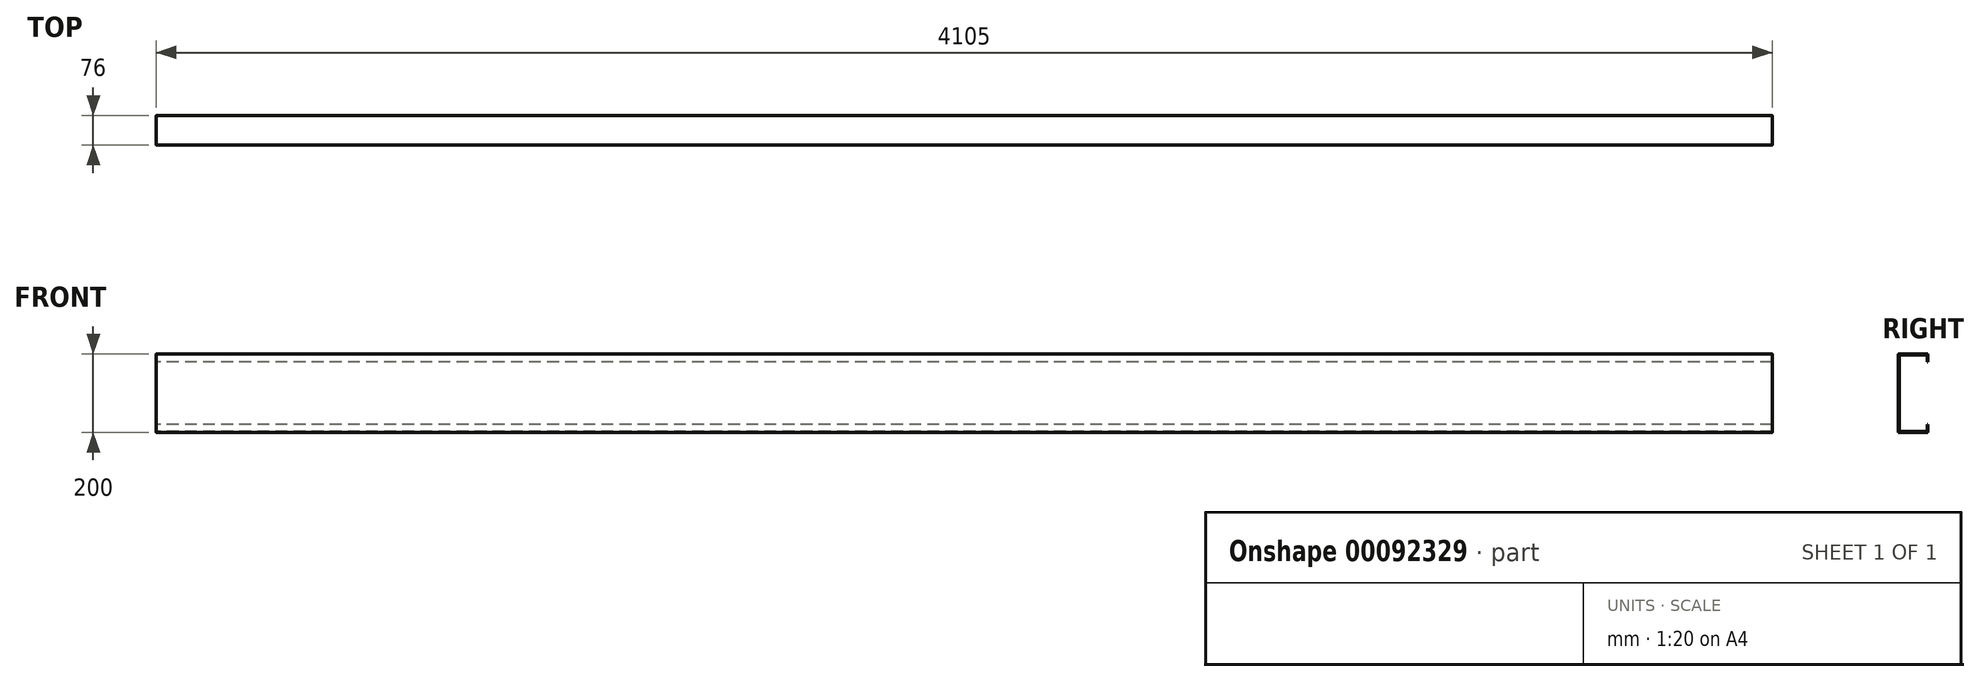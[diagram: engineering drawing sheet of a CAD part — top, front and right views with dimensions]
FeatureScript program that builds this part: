
annotation { "Feature Type Name" : "Feature", "Feature Type Description" : "" }
export const myFeature = defineFeature(function(context is Context, id is Id, definition is map)
    precondition{}
    {
        {
            var Q0;
            Q0=qCreatedBy(makeId("Right.planeOp"),FACE);
            var sketch = newSketch(context, id + "F0", { "sketchPlane" : qUnion([Q0])});
            skLineSegment(sketch, "E0", {"start": v(-2.4, 0) * mm, "end": v(-73.6, 0) * mm});
            skLineSegment(sketch, "E1", {"start": v(-76, 2.4) * mm, "end": v(-76, 197.6) * mm});
            skLineSegment(sketch, "E2", {"start": v(-73.6, 200) * mm, "end": v(-2.4, 200) * mm});
            skLineSegment(sketch, "E3", {"start": v(0, 200) * mm, "end": v(0, 197.6) * mm});
            skLineSegment(sketch, "E4", {"start": v(-4.8, 197.6) * mm, "end": v(-71.2, 197.6) * mm});
            skLineSegment(sketch, "E5", {"start": v(-73.6, 195.2) * mm, "end": v(-73.6, 4.8) * mm});
            skLineSegment(sketch, "E6", {"start": v(-71.2, 2.4) * mm, "end": v(-4.8, 2.4) * mm});
            skLineSegment(sketch, "E7", {"start": v(0, 2.4) * mm, "end": v(0, 0) * mm});
            skLineSegment(sketch, "E8", {"start": v(0, 197.6) * mm, "end": v(0, 180) * mm});
            skLineSegment(sketch, "E9", {"start": v(0, 180) * mm, "end": v(-2.4, 180) * mm});
            skLineSegment(sketch, "E10", {"start": v(-2.4, 180) * mm, "end": v(-2.4, 195.2) * mm});
            skLineSegment(sketch, "E11", {"start": v(0, 2.4) * mm, "end": v(0, 20) * mm});
            skLineSegment(sketch, "E12", {"start": v(0, 20) * mm, "end": v(-2.4, 20) * mm});
            skLineSegment(sketch, "E13", {"start": v(-2.4, 20) * mm, "end": v(-2.4, 4.8) * mm});
            skPoint(sketch, "E14.visualSharp", {"position": v(-76, 200) * mm});
            skArc(sketch, "E14.filletArc", {"start": v(-73.6, 200) * mm, "mid": v(-75.3, 199.3) * mm, "end": v(-76, 197.6) * mm});
            skArc(sketch, "E15.filletArc", {"start": v(-71.2, 197.6) * mm, "mid": v(-72.9, 196.9) * mm, "end": v(-73.6, 195.2) * mm});
            skPoint(sketch, "E16.visualSharp", {"position": v(-2.4, 197.6) * mm});
            skArc(sketch, "E16.filletArc", {"start": v(-2.4, 195.2) * mm, "mid": v(-3.1, 196.9) * mm, "end": v(-4.8, 197.6) * mm});
            skPoint(sketch, "E17.newPointA", {"position": v(0, 200) * mm});
            skPoint(sketch, "E17.newPointB", {"position": v(0, 197.6) * mm});
            skArc(sketch, "E17.filletArc", {"start": v(0, 197.6) * mm, "mid": v(-0.7, 199.3) * mm, "end": v(-2.4, 200) * mm});
            skPoint(sketch, "E18.visualSharp", {"position": v(-73.6, 2.4) * mm});
            skArc(sketch, "E18.filletArc", {"start": v(-73.6, 4.8) * mm, "mid": v(-72.9, 3.1) * mm, "end": v(-71.2, 2.4) * mm});
            skPoint(sketch, "E19.visualSharp", {"position": v(-76, 0) * mm});
            skArc(sketch, "E19.filletArc", {"start": v(-76, 2.4) * mm, "mid": v(-75.3, 0.7) * mm, "end": v(-73.6, 0) * mm});
            skPoint(sketch, "E20.newPointA", {"position": v(0, 0) * mm});
            skPoint(sketch, "E20.newPointB", {"position": v(0, 2.4) * mm});
            skArc(sketch, "E20.filletArc", {"start": v(-2.4, 0) * mm, "mid": v(-0.7, 0.7) * mm, "end": v(0, 2.4) * mm});
            skArc(sketch, "E21.filletArc", {"start": v(-4.8, 2.4) * mm, "mid": v(-3.1, 3.1) * mm, "end": v(-2.4, 4.8) * mm});
            skSolve(sketch);
        }
        {
            var Q0;
            Q0=qSketchRegion(id+"F0",true);
            extrude(context, id + "F1", {"entities" : qUnion([Q0]), "offsetDistance" : 25 * mm, "depth" : 4105 * mm});
        }
    });
